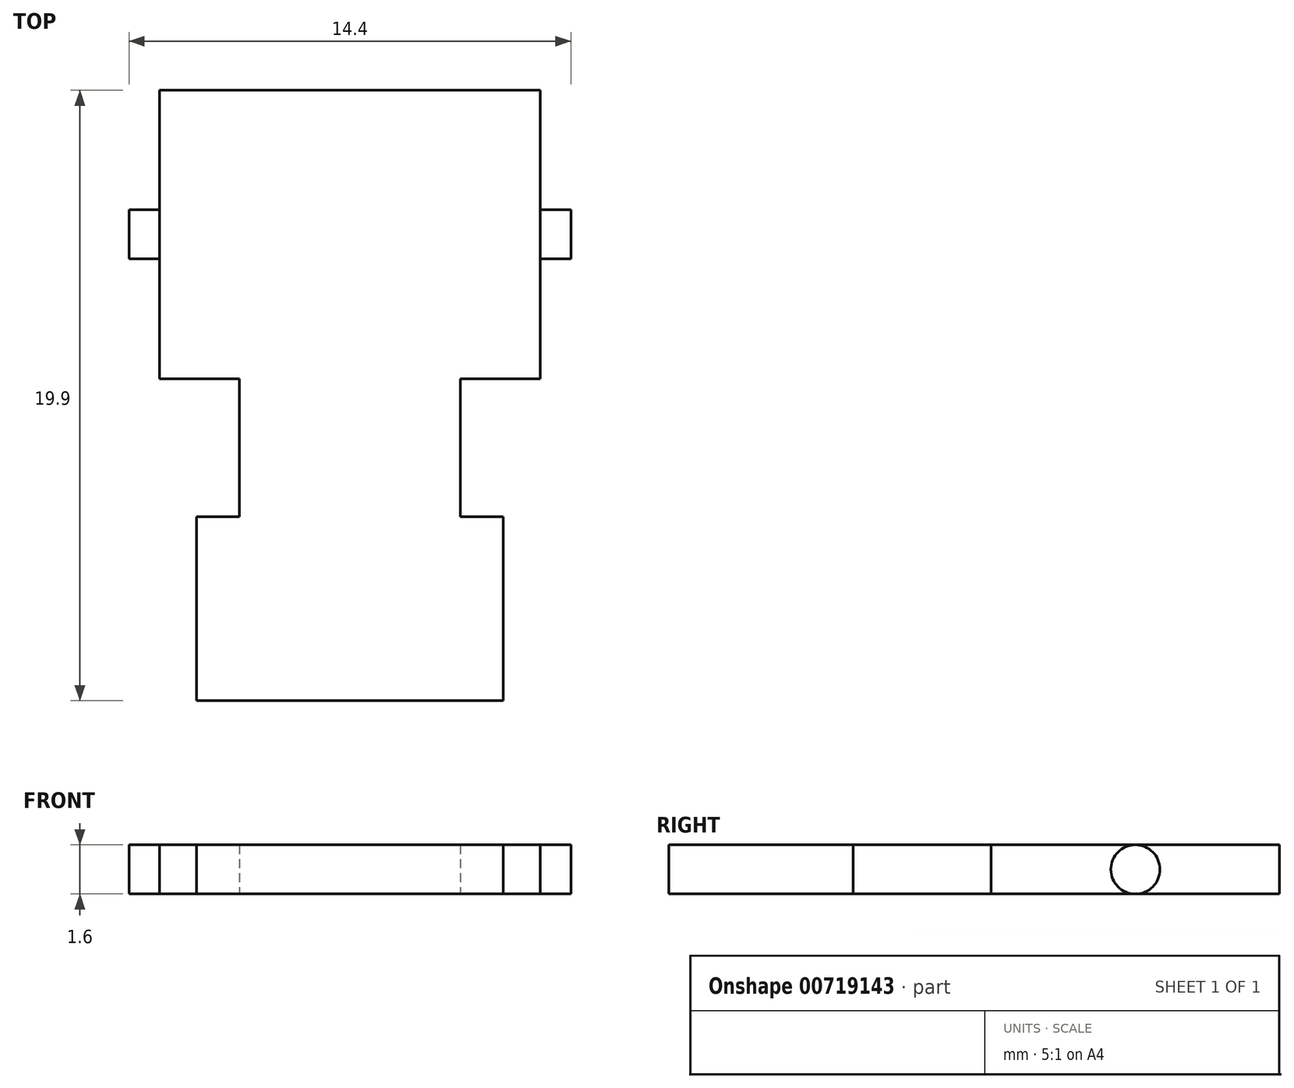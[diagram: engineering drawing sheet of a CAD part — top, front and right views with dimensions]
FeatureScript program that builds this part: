
annotation { "Feature Type Name" : "Feature", "Feature Type Description" : "" }
export const myFeature = defineFeature(function(context is Context, id is Id, definition is map)
    precondition{}
    {
        {
            var Q0;
            Q0=qCreatedBy(makeId("Top.planeOp"),FACE);
            var sketch = newSketch(context, id + "F0", { "sketchPlane" : qUnion([Q0])});
            skLineSegment(sketch, "E0.bottom", {"start": v(0, 0) * mm, "end": v(2.6, 0) * mm});
            skLineSegment(sketch, "E0.top", {"start": v(0, 9.4) * mm, "end": v(12.4, 9.4) * mm});
            skLineSegment(sketch, "E0.left", {"start": v(0, 0) * mm, "end": v(0, 3.9) * mm});
            skLineSegment(sketch, "E0.right", {"start": v(12.4, 0) * mm, "end": v(12.4, 3.9) * mm});
            skLineSegment(sketch, "E1", {"start": v(2.6, 0) * mm, "end": v(2.6, -4.5) * mm});
            skLineSegment(sketch, "E2", {"start": v(9.8, -4.5) * mm, "end": v(9.8, 0) * mm});
            skLineSegment(sketch, "E3.trimOffspring", {"start": v(9.8, 0) * mm, "end": v(12.4, 0) * mm});
            skLineSegment(sketch, "E4", {"start": v(6.2, 9.4) * mm, "end": v(6.2, 5.33) * mm, "construction": true});
            skLineSegment(sketch, "E5", {"start": v(1.2, -4.5) * mm, "end": v(2.6, -4.5) * mm});
            skLineSegment(sketch, "E6.trimOffspring", {"start": v(9.8, -4.5) * mm, "end": v(11.2, -4.5) * mm});
            skLineSegment(sketch, "E7", {"start": v(1.2, -10.5) * mm, "end": v(11.2, -10.5) * mm});
            skLineSegment(sketch, "E8", {"start": v(0, 5.5) * mm, "end": v(-1, 5.5) * mm});
            skLineSegment(sketch, "E9", {"start": v(-1, 5.5) * mm, "end": v(-1, 3.9) * mm});
            skLineSegment(sketch, "E10", {"start": v(-1, 3.9) * mm, "end": v(0, 3.9) * mm});
            skLineSegment(sketch, "E11", {"start": v(12.4, 5.5) * mm, "end": v(13.4, 5.5) * mm});
            skLineSegment(sketch, "E12", {"start": v(13.4, 5.5) * mm, "end": v(13.4, 3.9) * mm});
            skLineSegment(sketch, "E13", {"start": v(13.4, 3.9) * mm, "end": v(12.4, 3.9) * mm});
            skLineSegment(sketch, "E14.trimOffspring", {"start": v(0, 5.5) * mm, "end": v(0, 9.4) * mm});
            skLineSegment(sketch, "E15.trimOffspring", {"start": v(12.4, 5.5) * mm, "end": v(12.4, 9.4) * mm});
            skLineSegment(sketch, "E16", {"start": v(-1, 4.7) * mm, "end": v(2.65, 4.7) * mm, "construction": true});
            skLineSegment(sketch, "E17", {"start": v(1.2, -4.5) * mm, "end": v(1.2, -10.5) * mm});
            skLineSegment(sketch, "E18", {"start": v(11.2, -4.5) * mm, "end": v(11.2, -10.5) * mm});
            skSolve(sketch);
        }
        {
            var Q0;
            Q0 = qSketchRegion(id + "F0", true);
            extrude(context, id + "F1", {"entities" : qUnion([Q0]), "depth" : 1.6 * mm, "offsetDistance" : 25 * mm});
        }
        {
            var Q0;
            Q0=makeQuery(id+"F1.opExtrude","SWEPT_FACE",FACE,{"disambiguationData":[OSD([sQuery(id+"F0.wireOp",EDGE,"E9")])]});
            var sketch = newSketch(context, id + "F2", { "sketchPlane" : qUnion([Q0])});
            skCircle(sketch, "E19", {"center": v(-4.7, 0.8) * mm, "radius": 0.8 * mm});
            skPoint(sketch, "E19.centerSnap0", {"position": v(-5.5, 0.8) * mm});
            skLineSegment(sketch, "E20.bottom", {"start": v(-6.22, 2.5) * mm, "end": v(-3.07, 2.5) * mm});
            skLineSegment(sketch, "E20.top", {"start": v(-6.22, -0.72) * mm, "end": v(-3.07, -0.72) * mm});
            skLineSegment(sketch, "E20.left", {"start": v(-6.22, 2.5) * mm, "end": v(-6.22, -0.72) * mm});
            skLineSegment(sketch, "E20.right", {"start": v(-3.07, 2.5) * mm, "end": v(-3.07, -0.72) * mm});
            skSolve(sketch);
        }
        {
            var Q0;
            Q0 = qSketchRegion(id + "F2", true);
            var Q1;
            Q1=makeQuery(id+"F1.opExtrude","SWEPT_FACE",FACE,{"disambiguationData":[OSD([sQuery(id+"F0.wireOp",EDGE,"E0.left")])]});
            extrude(context, id + "F3", {"entities" : qUnion([Q0]), "operationType" : NewBodyOperationType.REMOVE, "endBound" : BoundingType.UP_TO_SURFACE, "oppositeDirection" : true, "depth" : 25 * mm, "endBoundEntityFace" : qUnion([Q1]), "offsetDistance" : 25 * mm});
        }
        {
            var Q0;
            Q0=makeQuery(id+"F1.opExtrude","SWEPT_FACE",FACE,{"disambiguationData":[OSD([sQuery(id+"F0.wireOp",EDGE,"E12")])]});
            var sketch = newSketch(context, id + "F4", { "sketchPlane" : qUnion([Q0])});
            skCircle(sketch, "E21", {"center": v(4.7, 0.8) * mm, "radius": 0.8 * mm});
            skPoint(sketch, "E21.centerSnap0", {"position": v(5.5, 0.8) * mm});
            skLineSegment(sketch, "E22.bottom", {"start": v(3.3, 2.22) * mm, "end": v(6.2, 2.22) * mm});
            skLineSegment(sketch, "E22.top", {"start": v(3.3, -0.74) * mm, "end": v(6.2, -0.74) * mm});
            skLineSegment(sketch, "E22.left", {"start": v(3.3, 2.22) * mm, "end": v(3.3, -0.74) * mm});
            skLineSegment(sketch, "E22.right", {"start": v(6.2, 2.22) * mm, "end": v(6.2, -0.74) * mm});
            skSolve(sketch);
        }
        {
            var Q0;
            Q0 = qSketchRegion(id + "F4", true);
            var Q1;
            Q1=makeQuery(id+"F1.opExtrude","SWEPT_FACE",FACE,{"disambiguationData":[OSD([sQuery(id+"F0.wireOp",EDGE,"E15.trimOffspring")])]});
            extrude(context, id + "F5", {"entities" : qUnion([Q0]), "operationType" : NewBodyOperationType.REMOVE, "endBound" : BoundingType.UP_TO_SURFACE, "oppositeDirection" : true, "depth" : 25 * mm, "endBoundEntityFace" : qUnion([Q1]), "offsetDistance" : 25 * mm});
        }
    });
